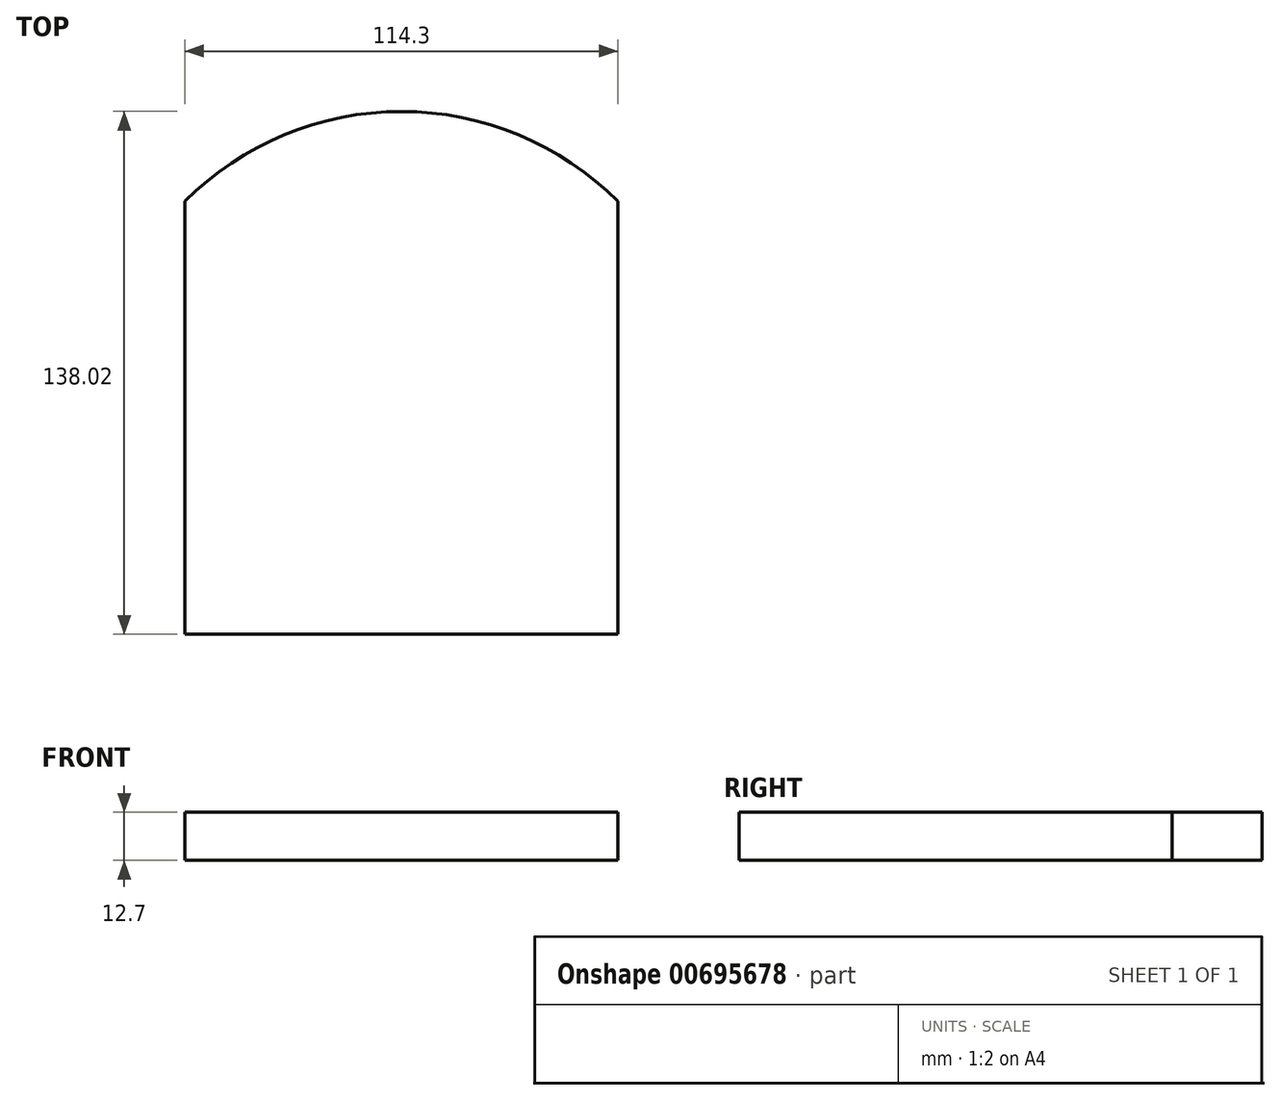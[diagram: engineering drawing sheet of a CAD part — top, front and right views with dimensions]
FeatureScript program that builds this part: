
annotation { "Feature Type Name" : "Feature", "Feature Type Description" : "" }
export const myFeature = defineFeature(function(context is Context, id is Id, definition is map)
    precondition{}
    {
        {
            var Q0;
            Q0=qCreatedBy(makeId("Top.planeOp"),FACE);
            var sketch = newSketch(context, id + "F0", { "sketchPlane" : qUnion([Q0])});
            skLineSegment(sketch, "E0.bottom", {"start": v(-113.1, -40.9) * mm, "end": v(1.2, -40.9) * mm});
            skLineSegment(sketch, "E0.left", {"start": v(-113.1, -40.9) * mm, "end": v(-113.1, 73.4) * mm});
            skLineSegment(sketch, "E0.right", {"start": v(1.2, -40.9) * mm, "end": v(1.2, 73.4) * mm});
            skArc(sketch, "E1", {"start": v(1.2, 73.4) * mm, "mid": v(-55.95, 97.12) * mm, "end": v(-113.1, 73.4) * mm});
            skSolve(sketch);
        }
        {
            var Q0;
            Q0 = qSketchRegion(id + "F0", true);
            extrude(context, id + "F1", {"entities" : qUnion([Q0]), "depth" : 12.7 * mm, "offsetDistance" : 25.4 * mm});
        }
    });
